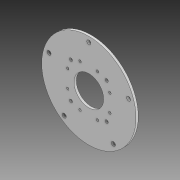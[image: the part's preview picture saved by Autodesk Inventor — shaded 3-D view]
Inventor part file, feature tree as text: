
AUTODESK INVENTOR PART (.ipt)
format: ipt  version: 2020 (Build 240168000, 168)  size: 170,496 bytes
history: native  units: mm
features: extrude x4, sketch x4
ambient origin geometry x8: Origin, YZ Plane, XZ Plane, XY Plane, X Axis, Y Axis, Z Axis, Center Point
bodies: Solid1 (feature_tree)
feature tree (8):
  extrude  "Extrusion1"  Depth=3.0mm
  extrude  "Extrusion2"  Depth=4.0mm
  extrude  "Extrusion3"  TaperAngle=0.0deg  [1 undecoded]
  extrude  "Extrusion4"  Depth=62.0mm
  sketch  "Sketch1"  dims[d0=3.0mm d1=0.0mm d2=39.0mm]
  sketch  "Sketch2"  dims[d3=47.0mm d4=4.0mm]
  sketch  "Sketch3"  dims[d5=0.0mm d6=0.0mm d7=0.0mm d8=0.0mm]
  sketch  "Sketch4"  dims[d9=60.0mm d10=3.2mm d11=80.0mm d13=360.0deg d15=0.0mm d16=0.0mm d23=110.0mm d24=95.0mm d25=62.0mm d26=80.0mm d27=5.3mm d28=50.0mm d30=360.0deg]
note: 1 required parameter value undecoded (feature->parameter linkage not recoverable at this tier; creation-order binding heuristic only, values carry confidence <= 0.55)
